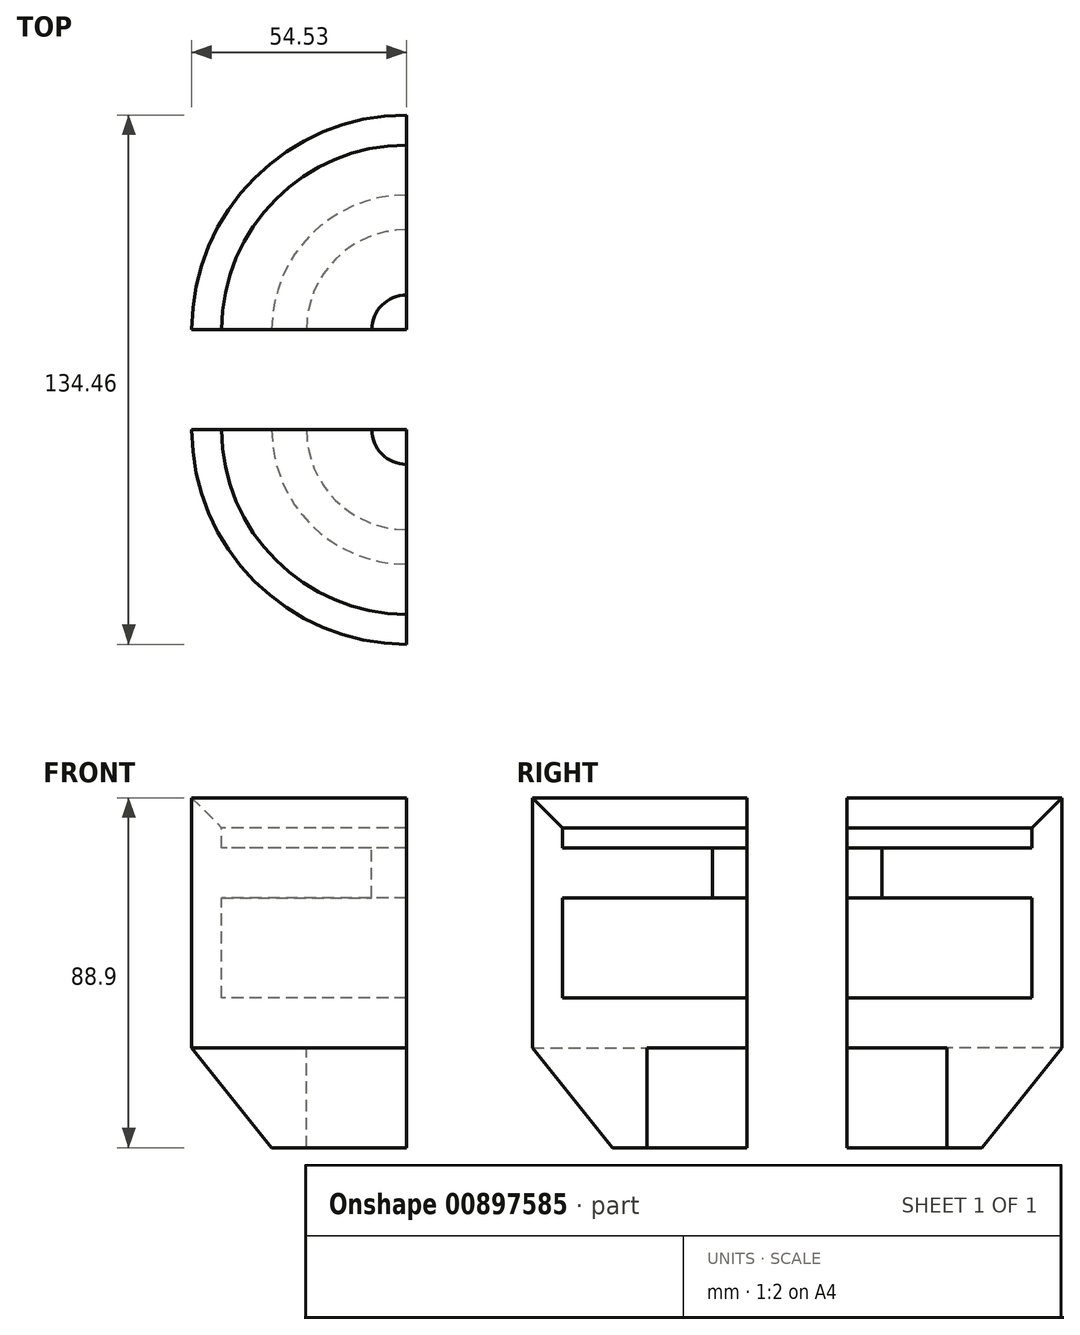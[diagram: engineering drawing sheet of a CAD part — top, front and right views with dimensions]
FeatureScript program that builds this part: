
annotation { "Feature Type Name" : "Feature", "Feature Type Description" : "" }
export const myFeature = defineFeature(function(context is Context, id is Id, definition is map)
    precondition{}
    {
        {
            var Q0;
            Q0=qCreatedBy(makeId("Front.planeOp"),FACE);
            var sketch = newSketch(context, id + "F0", { "sketchPlane" : qUnion([Q0])});
            skLineSegment(sketch, "E0", {"start": v(0, 0) * mm, "end": v(0, 25.4) * mm});
            skLineSegment(sketch, "E1", {"start": v(0, 25.4) * mm, "end": v(25.4, 25.4) * mm});
            skLineSegment(sketch, "E2", {"start": v(25.4, 25.4) * mm, "end": v(25.4, 38.1) * mm});
            skLineSegment(sketch, "E3", {"start": v(25.4, 38.1) * mm, "end": v(-21.51, 38.1) * mm});
            skLineSegment(sketch, "E4", {"start": v(-21.51, 38.1) * mm, "end": v(-21.51, 63.5) * mm});
            skLineSegment(sketch, "E5", {"start": v(-21.51, 63.5) * mm, "end": v(16.59, 63.5) * mm});
            skLineSegment(sketch, "E6", {"start": v(16.59, 63.5) * mm, "end": v(16.59, 76.2) * mm});
            skLineSegment(sketch, "E7", {"start": v(16.59, 76.2) * mm, "end": v(-21.51, 76.2) * mm});
            skLineSegment(sketch, "E8", {"start": v(-21.51, 76.2) * mm, "end": v(-21.51, 88.9) * mm});
            skLineSegment(sketch, "E9", {"start": v(-21.51, 88.9) * mm, "end": v(-29.13, 88.9) * mm});
            skLineSegment(sketch, "E10", {"start": v(-29.13, 88.9) * mm, "end": v(-29.13, 25.4) * mm});
            skLineSegment(sketch, "E11", {"start": v(-29.13, 25.4) * mm, "end": v(-8.81, 0) * mm});
            skLineSegment(sketch, "E12", {"start": v(-8.81, 0) * mm, "end": v(0, 0) * mm});
            skSolve(sketch);
        }
        {
            var Q0;
            Q0 = qSketchRegion(id + "F0", true);
            var Q1;
            Q1=sQuery(id+"F0.wireOp",EDGE,"E2");
            revolve(context, id + "F1", {"surfaceOperationType" : NewSurfaceOperationType.NEW, "entities" : qUnion([Q0]), "axis" : qUnion([Q1]), "revolveType" : RevolveType.ONE_DIRECTION, "angle" : 90 * degree});
        }
        {
            var Q0;
            Q0=makeQuery(id+"F1.opRevolve","SWEPT_EDGE",EDGE,{"disambiguationData":[OSD([sQuery(id+"F0.wireOp",EDGE,"E8"),sQuery(id+"F0.wireOp",EDGE,"E9")])]});
            chamfer(context, id + "F2", {"entities" : qUnion([Q0]), "width" : 7.62 * mm, "tangentPropagation" : true});
        }
        {
            var Q0;
            Q0=makeQuery(id+"F1.opRevolve","CAP_FACE",FACE,{"disambiguationData":[OSD([sQuery(id+"F0.wireOp",EDGE,"E0"),sQuery(id+"F0.wireOp",EDGE,"E1"),sQuery(id+"F0.wireOp",EDGE,"E2"),sQuery(id+"F0.wireOp",EDGE,"E3"),sQuery(id+"F0.wireOp",EDGE,"E4"),sQuery(id+"F0.wireOp",EDGE,"E5"),sQuery(id+"F0.wireOp",EDGE,"E6"),sQuery(id+"F0.wireOp",EDGE,"E7"),sQuery(id+"F0.wireOp",EDGE,"E8"),sQuery(id+"F0.wireOp",EDGE,"E9"),sQuery(id+"F0.wireOp",EDGE,"E10"),sQuery(id+"F0.wireOp",EDGE,"E11"),sQuery(id+"F0.wireOp",EDGE,"E12")])],"isStart":true});
            cPlane(context, id + "F3", {"entities" : qUnion([Q0]), "cplaneType" : CPlaneType.OFFSET, "offset" : 12.7 * mm, "width" : 152.4 * mm, "height" : 152.4 * mm});
        }
        {
            var Q0;
            Q0=makeQuery(id+"F1.opRevolve","SWEPT_BODY",BODY,{"disambiguationData":[OSD([sQuery(id+"F0.wireOp",EDGE,"E0"),sQuery(id+"F0.wireOp",EDGE,"E1"),sQuery(id+"F0.wireOp",EDGE,"E2"),sQuery(id+"F0.wireOp",EDGE,"E3"),sQuery(id+"F0.wireOp",EDGE,"E4"),sQuery(id+"F0.wireOp",EDGE,"E5"),sQuery(id+"F0.wireOp",EDGE,"E6"),sQuery(id+"F0.wireOp",EDGE,"E7"),sQuery(id+"F0.wireOp",EDGE,"E8"),sQuery(id+"F0.wireOp",EDGE,"E9"),sQuery(id+"F0.wireOp",EDGE,"E10"),sQuery(id+"F0.wireOp",EDGE,"E11"),sQuery(id+"F0.wireOp",EDGE,"E12")])]});
            var Q1;
            Q1=qCreatedBy(id+"F3.planeOp",FACE);
            mirror(context, id + "F4", {"entities" : qUnion([Q0]), "mirrorPlane" : qUnion([Q1])});
        }
    });
